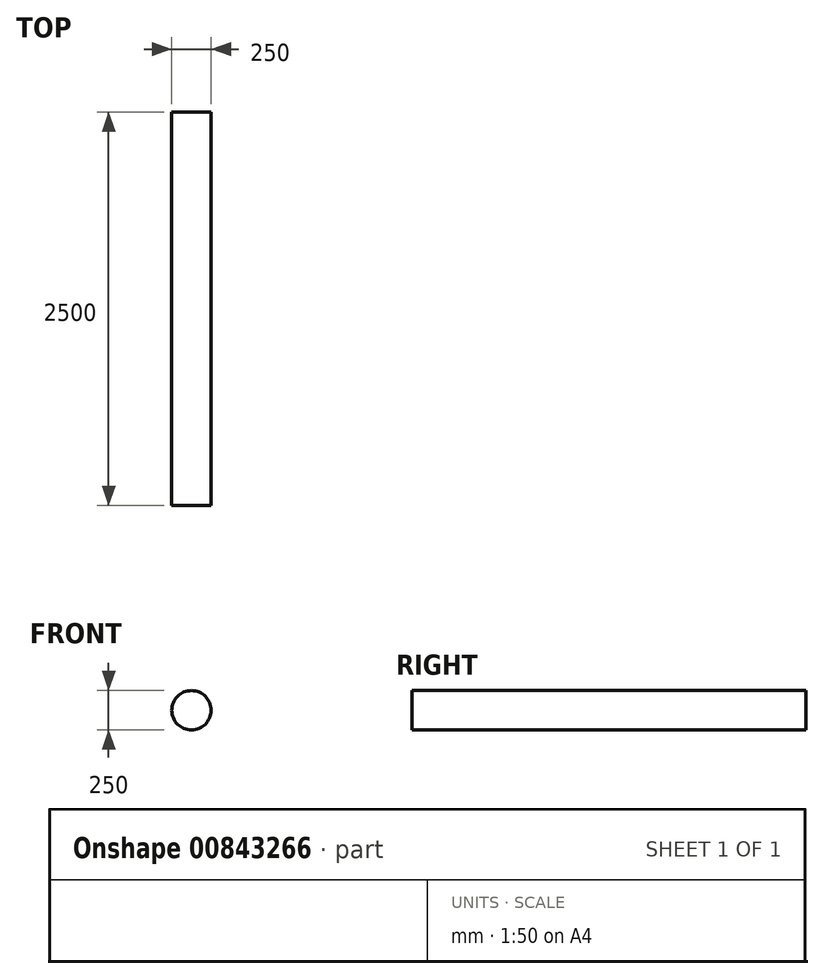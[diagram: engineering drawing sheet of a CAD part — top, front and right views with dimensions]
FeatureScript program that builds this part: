
annotation { "Feature Type Name" : "Feature", "Feature Type Description" : "" }
export const myFeature = defineFeature(function(context is Context, id is Id, definition is map)
    precondition{}
    {
        {
            var Q0;
            Q0=qCreatedBy(makeId("Front.planeOp"),FACE);
            var sketch = newSketch(context, id + "F0", { "sketchPlane" : qUnion([Q0])});
            skCircle(sketch, "E0", {"center": v(0, 0) * mm, "radius": 125 * mm});
            skSolve(sketch);
        }
        {
            var Q0;
            Q0=makeQuery(id+"F0.imprint","IMPRINT",FACE,{"disambiguationData":[TD([[makeQuery(id+"F0.imprint","IMPRINT",EDGE,{"derivedFrom":sQuery(id+"F0.wireOp",EDGE,"E0")}),1.0]])]});
            extrude(context, id + "F1", {"entities" : qUnion([Q0]), "endBound" : BoundingType.SYMMETRIC, "oppositeDirection" : true, "depth" : 2500 * mm, "offsetDistance" : 25 * mm});
        }
    });
